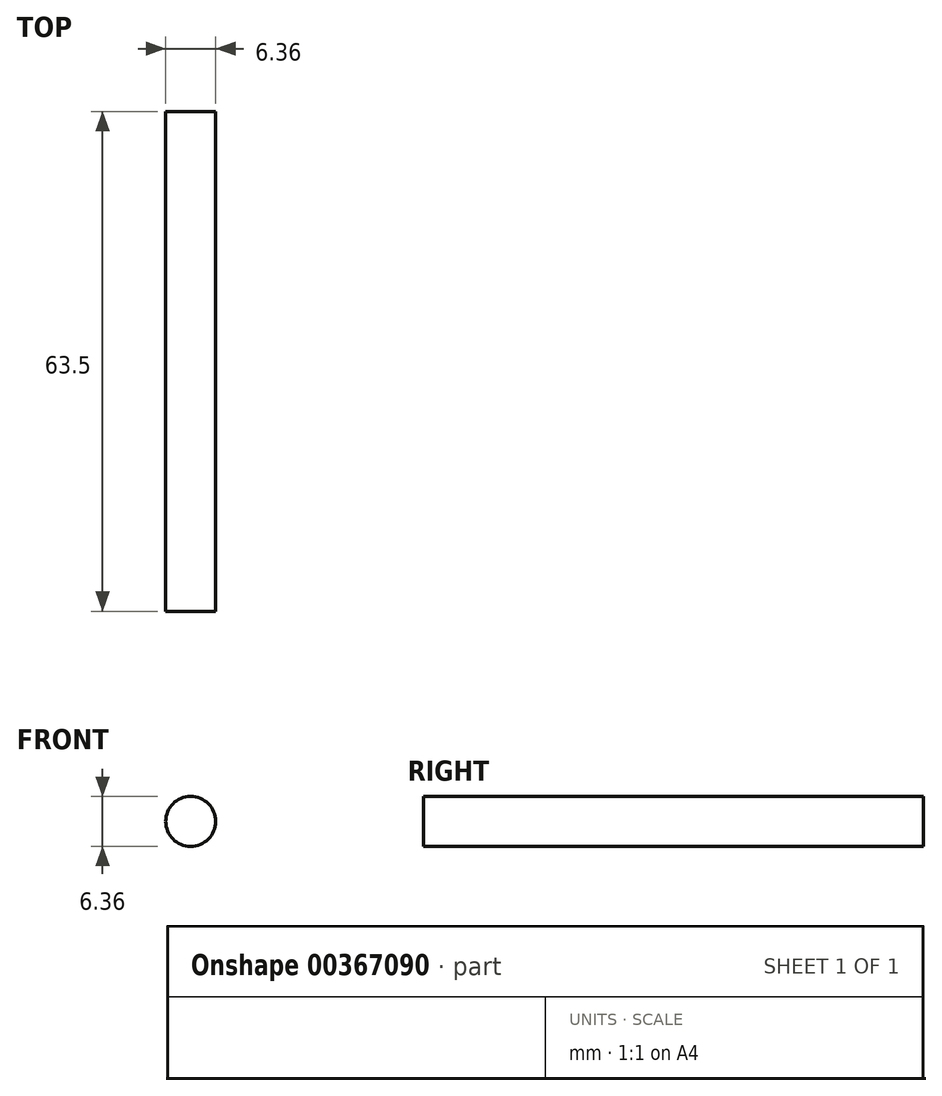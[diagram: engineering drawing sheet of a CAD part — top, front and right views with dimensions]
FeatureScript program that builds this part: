
annotation { "Feature Type Name" : "Feature", "Feature Type Description" : "" }
export const myFeature = defineFeature(function(context is Context, id is Id, definition is map)
    precondition{}
    {
        {
            var Q0;
            Q0=qCreatedBy(makeId("Front.planeOp"),FACE);
            var sketch = newSketch(context, id + "F0", { "sketchPlane" : qUnion([Q0])});
            skCircle(sketch, "E0", {"center": v(0, 0) * mm, "radius": 3.18 * mm});
            skSolve(sketch);
        }
        {
            var Q0;
            Q0=makeQuery(id+"F0.imprint","IMPRINT",FACE,{"disambiguationData":[TD([[makeQuery(id+"F0.imprint","IMPRINT",EDGE,{"derivedFrom":sQuery(id+"F0.wireOp",EDGE,"E0")}),1.0]])]});
            extrude(context, id + "F1", {"entities" : qUnion([Q0]), "depth" : 63.5 * mm});
        }
    });
